# Revit family: console with 2 cutouts for countertop basin ground
name_source: partatom
category: Furniture
units: mm (PartAtom-declared; Revit-internal decimal feet)

## family parameters
Always vertical = No
Cut with Voids When Loaded = No
OmniClass Number = 23.19.31.17.11
Room Calculation Point = No
Shared = Yes
Work Plane-Based = No

## types (16) — shared parameters
BIMOBJECT = Region Set
CATALOG = Hansgrohe
DESIGN = Germany
ETIM = EC011381 | Bathroom furniture set
IFC = Furnishing element
LC = 115
MASTERFORMAT = 12 35 30.23 | Bathroom Casework
Manufacturer = Hansgrohe
NBSYN = $BASENUMBER.-$ARTNR.-$SURFACE.-$LODLEVEL.
NN = Console with 2 cutouts for countertop basin ground
OBJECTTYPE = Object (single object)
OMNICLASS = 23-19 31 17 11 | Bathroom Units
PRODUCTFAMILY = Xelu Q
PRODUCTGROUP = console
PRODUCTURL = https://pro.hansgrohe.com
REGIONSET = Worldwide
UNICLASS2015 = Pr_40_20_76_94 | Vanity units
UNIFORMATII = E2010 | Fixed Furnishings
UNSPSC = 56 | Furniture and Furnishings

## per-type parameters (varying)
| type | ARTNR | BASENUMBER | GTINCODE | L | L1 | LINA | LODLEVEL | Model | NAME | NB | PERMALINK | SPECIFICATION | SURFACE | WEIGHT |
| Console 1360_550 with 2 cutouts for countertop basin ground 500_480-54099050-GLOSSY_WHITE-200 | 54099050 | Console 1360/550 with 2 cutouts for countertop basin ground 500/480 | 4059625457337 | 1360 | 450 | Console 1360/550 with 2 cutouts for countertop basin ground 500/480-54099050-GLOSSY_WHITE-200 | 200 | Console 1360/550 with 2 cutouts for countertop basin ground 500/480-54099050-GLOSSY_WHITE-200 | Xelu Q Console 1360/550 with 2 cutouts for countertop basin ground 500/480 | Console 1360/550 with 2 cutouts for countertop basin ground 500/480-54099050-GLOSSY_WHITE-200 | 54099XXX | Surfaces:    - 54099050 High Gloss White  - 54099910 Diamond Matt Grey  - 54099230 Natural Oak  - 54099630 Dark Walnut      Specification: | GLOSSY_WHITE | 7.5 |
| Console 1360_550 with 2 cutouts for countertop basin ground 500_480-54099050-GLOSSY_WHITE-400 | 54099050 | Console 1360/550 with 2 cutouts for countertop basin ground 500/480 | 4059625457337 | 1360 | 450 | Console 1360/550 with 2 cutouts for countertop basin ground 500/480-54099050-GLOSSY_WHITE-400 | 400 | Console 1360/550 with 2 cutouts for countertop basin ground 500/480-54099050-GLOSSY_WHITE-400 | Xelu Q Console 1360/550 with 2 cutouts for countertop basin ground 500/480 | Console 1360/550 with 2 cutouts for countertop basin ground 500/480-54099050-GLOSSY_WHITE-400 | 54099XXX | Surfaces:    - 54099050 High Gloss White  - 54099910 Diamond Matt Grey  - 54099230 Natural Oak  - 54099630 Dark Walnut      Specification: | GLOSSY_WHITE | 7.5 |
| Console 1360_550 with 2 cutouts for countertop basin ground 500_480-54099230-NATURAL_OAK-200 | 54099230 | Console 1360/550 with 2 cutouts for countertop basin ground 500/480 | 4059625457337 | 1360 | 450 | Console 1360/550 with 2 cutouts for countertop basin ground 500/480-54099230-NATURAL_OAK-200 | 200 | Console 1360/550 with 2 cutouts for countertop basin ground 500/480-54099230-NATURAL_OAK-200 | Xelu Q Console 1360/550 with 2 cutouts for countertop basin ground 500/480 | Console 1360/550 with 2 cutouts for countertop basin ground 500/480-54099230-NATURAL_OAK-200 | 54099XXX | Surfaces:    - 54099050 High Gloss White  - 54099910 Diamond Matt Grey  - 54099230 Natural Oak  - 54099630 Dark Walnut      Specification: | NATURAL_OAK | 7.5 |
| Console 1360_550 with 2 cutouts for countertop basin ground 500_480-54099230-NATURAL_OAK-400 | 54099230 | Console 1360/550 with 2 cutouts for countertop basin ground 500/480 | 4059625457337 | 1360 | 450 | Console 1360/550 with 2 cutouts for countertop basin ground 500/480-54099230-NATURAL_OAK-400 | 400 | Console 1360/550 with 2 cutouts for countertop basin ground 500/480-54099230-NATURAL_OAK-400 | Xelu Q Console 1360/550 with 2 cutouts for countertop basin ground 500/480 | Console 1360/550 with 2 cutouts for countertop basin ground 500/480-54099230-NATURAL_OAK-400 | 54099XXX | Surfaces:    - 54099050 High Gloss White  - 54099910 Diamond Matt Grey  - 54099230 Natural Oak  - 54099630 Dark Walnut      Specification: | NATURAL_OAK | 7.5 |
| Console 1360_550 with 2 cutouts for countertop basin ground 500_480-54099630-DARK_WALNUT-200 | 54099630 | Console 1360/550 with 2 cutouts for countertop basin ground 500/480 | 4059625457337 | 1360 | 450 | Console 1360/550 with 2 cutouts for countertop basin ground 500/480-54099630-DARK_WALNUT-200 | 200 | Console 1360/550 with 2 cutouts for countertop basin ground 500/480-54099630-DARK_WALNUT-200 | Xelu Q Console 1360/550 with 2 cutouts for countertop basin ground 500/480 | Console 1360/550 with 2 cutouts for countertop basin ground 500/480-54099630-DARK_WALNUT-200 | 54099XXX | Surfaces:    - 54099050 High Gloss White  - 54099910 Diamond Matt Grey  - 54099230 Natural Oak  - 54099630 Dark Walnut      Specification: | DARK_WALNUT | 7.5 |
| Console 1360_550 with 2 cutouts for countertop basin ground 500_480-54099630-DARK_WALNUT-400 | 54099630 | Console 1360/550 with 2 cutouts for countertop basin ground 500/480 | 4059625457337 | 1360 | 450 | Console 1360/550 with 2 cutouts for countertop basin ground 500/480-54099630-DARK_WALNUT-400 | 400 | Console 1360/550 with 2 cutouts for countertop basin ground 500/480-54099630-DARK_WALNUT-400 | Xelu Q Console 1360/550 with 2 cutouts for countertop basin ground 500/480 | Console 1360/550 with 2 cutouts for countertop basin ground 500/480-54099630-DARK_WALNUT-400 | 54099XXX | Surfaces:    - 54099050 High Gloss White  - 54099910 Diamond Matt Grey  - 54099230 Natural Oak  - 54099630 Dark Walnut      Specification: | DARK_WALNUT | 7.5 |
| Console 1360_550 with 2 cutouts for countertop basin ground 500_480-54099910-DIAMOND_GREY-200 | 54099910 | Console 1360/550 with 2 cutouts for countertop basin ground 500/480 | 4059625457337 | 1360 | 450 | Console 1360/550 with 2 cutouts for countertop basin ground 500/480-54099910-DIAMOND_GREY-200 | 200 | Console 1360/550 with 2 cutouts for countertop basin ground 500/480-54099910-DIAMOND_GREY-200 | Xelu Q Console 1360/550 with 2 cutouts for countertop basin ground 500/480 | Console 1360/550 with 2 cutouts for countertop basin ground 500/480-54099910-DIAMOND_GREY-200 | 54099XXX | Surfaces:    - 54099050 High Gloss White  - 54099910 Diamond Matt Grey  - 54099230 Natural Oak  - 54099630 Dark Walnut      Specification: | DIAMOND_GREY | 7.5 |
| Console 1360_550 with 2 cutouts for countertop basin ground 500_480-54099910-DIAMOND_GREY-400 | 54099910 | Console 1360/550 with 2 cutouts for countertop basin ground 500/480 | 4059625457337 | 1360 | 450 | Console 1360/550 with 2 cutouts for countertop basin ground 500/480-54099910-DIAMOND_GREY-400 | 400 | Console 1360/550 with 2 cutouts for countertop basin ground 500/480-54099910-DIAMOND_GREY-400 | Xelu Q Console 1360/550 with 2 cutouts for countertop basin ground 500/480 | Console 1360/550 with 2 cutouts for countertop basin ground 500/480-54099910-DIAMOND_GREY-400 | 54099XXX | Surfaces:    - 54099050 High Gloss White  - 54099910 Diamond Matt Grey  - 54099230 Natural Oak  - 54099630 Dark Walnut      Specification: | DIAMOND_GREY | 7.5 |
| Console 1560_550 with 2 cutouts for countertop basin ground 600_480-54112050-GLOSSY_WHITE-200 | 54112050 | Console 1560/550 with 2 cutouts for countertop basin ground 600/480 | 4059625457573 | 1560 | 550 | Console 1560/550 with 2 cutouts for countertop basin ground 600/480-54112050-GLOSSY_WHITE-200 | 200 | Console 1560/550 with 2 cutouts for countertop basin ground 600/480-54112050-GLOSSY_WHITE-200 | Xelu Q Console 1560/550 with 2 cutouts for countertop basin ground 600/480 | Console 1560/550 with 2 cutouts for countertop basin ground 600/480-54112050-GLOSSY_WHITE-200 | 54112XXX | Surfaces:    - 54112050 High Gloss White  - 54112910 Diamond Matt Grey  - 54112230 Natural Oak  - 54112630 Dark Walnut      Specification: | GLOSSY_WHITE | 8.8 |
| Console 1560_550 with 2 cutouts for countertop basin ground 600_480-54112050-GLOSSY_WHITE-400 | 54112050 | Console 1560/550 with 2 cutouts for countertop basin ground 600/480 | 4059625457573 | 1560 | 550 | Console 1560/550 with 2 cutouts for countertop basin ground 600/480-54112050-GLOSSY_WHITE-400 | 400 | Console 1560/550 with 2 cutouts for countertop basin ground 600/480-54112050-GLOSSY_WHITE-400 | Xelu Q Console 1560/550 with 2 cutouts for countertop basin ground 600/480 | Console 1560/550 with 2 cutouts for countertop basin ground 600/480-54112050-GLOSSY_WHITE-400 | 54112XXX | Surfaces:    - 54112050 High Gloss White  - 54112910 Diamond Matt Grey  - 54112230 Natural Oak  - 54112630 Dark Walnut      Specification: | GLOSSY_WHITE | 8.8 |
| Console 1560_550 with 2 cutouts for countertop basin ground 600_480-54112230-NATURAL_OAK-200 | 54112230 | Console 1560/550 with 2 cutouts for countertop basin ground 600/480 | 4059625457573 | 1560 | 550 | Console 1560/550 with 2 cutouts for countertop basin ground 600/480-54112230-NATURAL_OAK-200 | 200 | Console 1560/550 with 2 cutouts for countertop basin ground 600/480-54112230-NATURAL_OAK-200 | Xelu Q Console 1560/550 with 2 cutouts for countertop basin ground 600/480 | Console 1560/550 with 2 cutouts for countertop basin ground 600/480-54112230-NATURAL_OAK-200 | 54112XXX | Surfaces:    - 54112050 High Gloss White  - 54112910 Diamond Matt Grey  - 54112230 Natural Oak  - 54112630 Dark Walnut      Specification: | NATURAL_OAK | 8.8 |
| Console 1560_550 with 2 cutouts for countertop basin ground 600_480-54112230-NATURAL_OAK-400 | 54112230 | Console 1560/550 with 2 cutouts for countertop basin ground 600/480 | 4059625457573 | 1560 | 550 | Console 1560/550 with 2 cutouts for countertop basin ground 600/480-54112230-NATURAL_OAK-400 | 400 | Console 1560/550 with 2 cutouts for countertop basin ground 600/480-54112230-NATURAL_OAK-400 | Xelu Q Console 1560/550 with 2 cutouts for countertop basin ground 600/480 | Console 1560/550 with 2 cutouts for countertop basin ground 600/480-54112230-NATURAL_OAK-400 | 54112XXX | Surfaces:    - 54112050 High Gloss White  - 54112910 Diamond Matt Grey  - 54112230 Natural Oak  - 54112630 Dark Walnut      Specification: | NATURAL_OAK | 8.8 |
| Console 1560_550 with 2 cutouts for countertop basin ground 600_480-54112630-DARK_WALNUT-200 | 54112630 | Console 1560/550 with 2 cutouts for countertop basin ground 600/480 | 4059625457573 | 1560 | 550 | Console 1560/550 with 2 cutouts for countertop basin ground 600/480-54112630-DARK_WALNUT-200 | 200 | Console 1560/550 with 2 cutouts for countertop basin ground 600/480-54112630-DARK_WALNUT-200 | Xelu Q Console 1560/550 with 2 cutouts for countertop basin ground 600/480 | Console 1560/550 with 2 cutouts for countertop basin ground 600/480-54112630-DARK_WALNUT-200 | 54112XXX | Surfaces:    - 54112050 High Gloss White  - 54112910 Diamond Matt Grey  - 54112230 Natural Oak  - 54112630 Dark Walnut      Specification: | DARK_WALNUT | 8.8 |
| Console 1560_550 with 2 cutouts for countertop basin ground 600_480-54112630-DARK_WALNUT-400 | 54112630 | Console 1560/550 with 2 cutouts for countertop basin ground 600/480 | 4059625457573 | 1560 | 550 | Console 1560/550 with 2 cutouts for countertop basin ground 600/480-54112630-DARK_WALNUT-400 | 400 | Console 1560/550 with 2 cutouts for countertop basin ground 600/480-54112630-DARK_WALNUT-400 | Xelu Q Console 1560/550 with 2 cutouts for countertop basin ground 600/480 | Console 1560/550 with 2 cutouts for countertop basin ground 600/480-54112630-DARK_WALNUT-400 | 54112XXX | Surfaces:    - 54112050 High Gloss White  - 54112910 Diamond Matt Grey  - 54112230 Natural Oak  - 54112630 Dark Walnut      Specification: | DARK_WALNUT | 8.8 |
| Console 1560_550 with 2 cutouts for countertop basin ground 600_480-54112910-DIAMOND_GREY-200 | 54112910 | Console 1560/550 with 2 cutouts for countertop basin ground 600/480 | 4059625457573 | 1560 | 550 | Console 1560/550 with 2 cutouts for countertop basin ground 600/480-54112910-DIAMOND_GREY-200 | 200 | Console 1560/550 with 2 cutouts for countertop basin ground 600/480-54112910-DIAMOND_GREY-200 | Xelu Q Console 1560/550 with 2 cutouts for countertop basin ground 600/480 | Console 1560/550 with 2 cutouts for countertop basin ground 600/480-54112910-DIAMOND_GREY-200 | 54112XXX | Surfaces:    - 54112050 High Gloss White  - 54112910 Diamond Matt Grey  - 54112230 Natural Oak  - 54112630 Dark Walnut      Specification: | DIAMOND_GREY | 8.8 |
| Console 1560_550 with 2 cutouts for countertop basin ground 600_480-54112910-DIAMOND_GREY-400 | 54112910 | Console 1560/550 with 2 cutouts for countertop basin ground 600/480 | 4059625457573 | 1560 | 550 | Console 1560/550 with 2 cutouts for countertop basin ground 600/480-54112910-DIAMOND_GREY-400 | 400 | Console 1560/550 with 2 cutouts for countertop basin ground 600/480-54112910-DIAMOND_GREY-400 | Xelu Q Console 1560/550 with 2 cutouts for countertop basin ground 600/480 | Console 1560/550 with 2 cutouts for countertop basin ground 600/480-54112910-DIAMOND_GREY-400 | 54112XXX | Surfaces:    - 54112050 High Gloss White  - 54112910 Diamond Matt Grey  - 54112230 Natural Oak  - 54112630 Dark Walnut      Specification: | DIAMOND_GREY | 8.8 |

type visibility flags: 16 boolean params named "<type name>_RX0RY0RZ0TX0TY0TZ0_V" — each type sets only its own to Yes (folded from table)

## geometry (parser evidence)
native form markers: Sweep x56
no freeform markers — native parametric forms only
